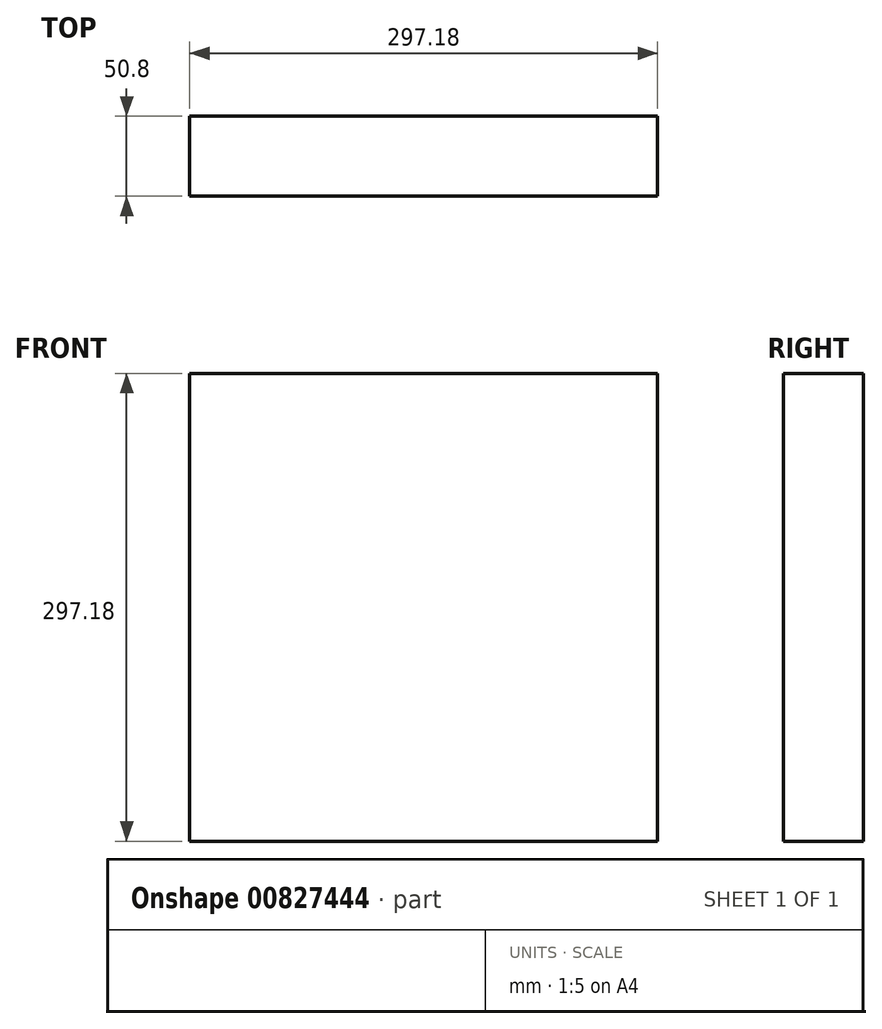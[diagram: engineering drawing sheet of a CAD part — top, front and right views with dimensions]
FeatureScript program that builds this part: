
annotation { "Feature Type Name" : "Feature", "Feature Type Description" : "" }
export const myFeature = defineFeature(function(context is Context, id is Id, definition is map)
    precondition{}
    {
        {
            var Q0;
            Q0=qCreatedBy(makeId("Front.planeOp"),FACE);
            var sketch = newSketch(context, id + "F0", { "sketchPlane" : qUnion([Q0])});
            skLineSegment(sketch, "E0.bottom", {"start": v(-148.6, 148.59) * mm, "end": v(148.6, 148.59) * mm});
            skLineSegment(sketch, "E0.top", {"start": v(-148.6, -148.59) * mm, "end": v(148.6, -148.59) * mm});
            skLineSegment(sketch, "E0.left", {"start": v(-148.6, 148.59) * mm, "end": v(-148.6, -148.59) * mm});
            skLineSegment(sketch, "E0.right", {"start": v(148.6, 148.59) * mm, "end": v(148.6, -148.59) * mm});
            skPoint(sketch, "E0.middle", {"position": v(0, 0) * mm});
            skSolve(sketch);
        }
        {
            var Q0;
            Q0=makeQuery(id+"F0.imprint","IMPRINT",FACE,{"disambiguationData":[TD([[makeQuery(id+"F0.imprint","IMPRINT",EDGE,{"derivedFrom":sQuery(id+"F0.wireOp",EDGE,"E0.bottom")}),-1.0]])]});
            extrude(context, id + "F1", {"entities" : qUnion([Q0]), "endBound" : BoundingType.SYMMETRIC, "depth" : 50.8 * mm, "offsetDistance" : 25.4 * mm});
        }
    });
